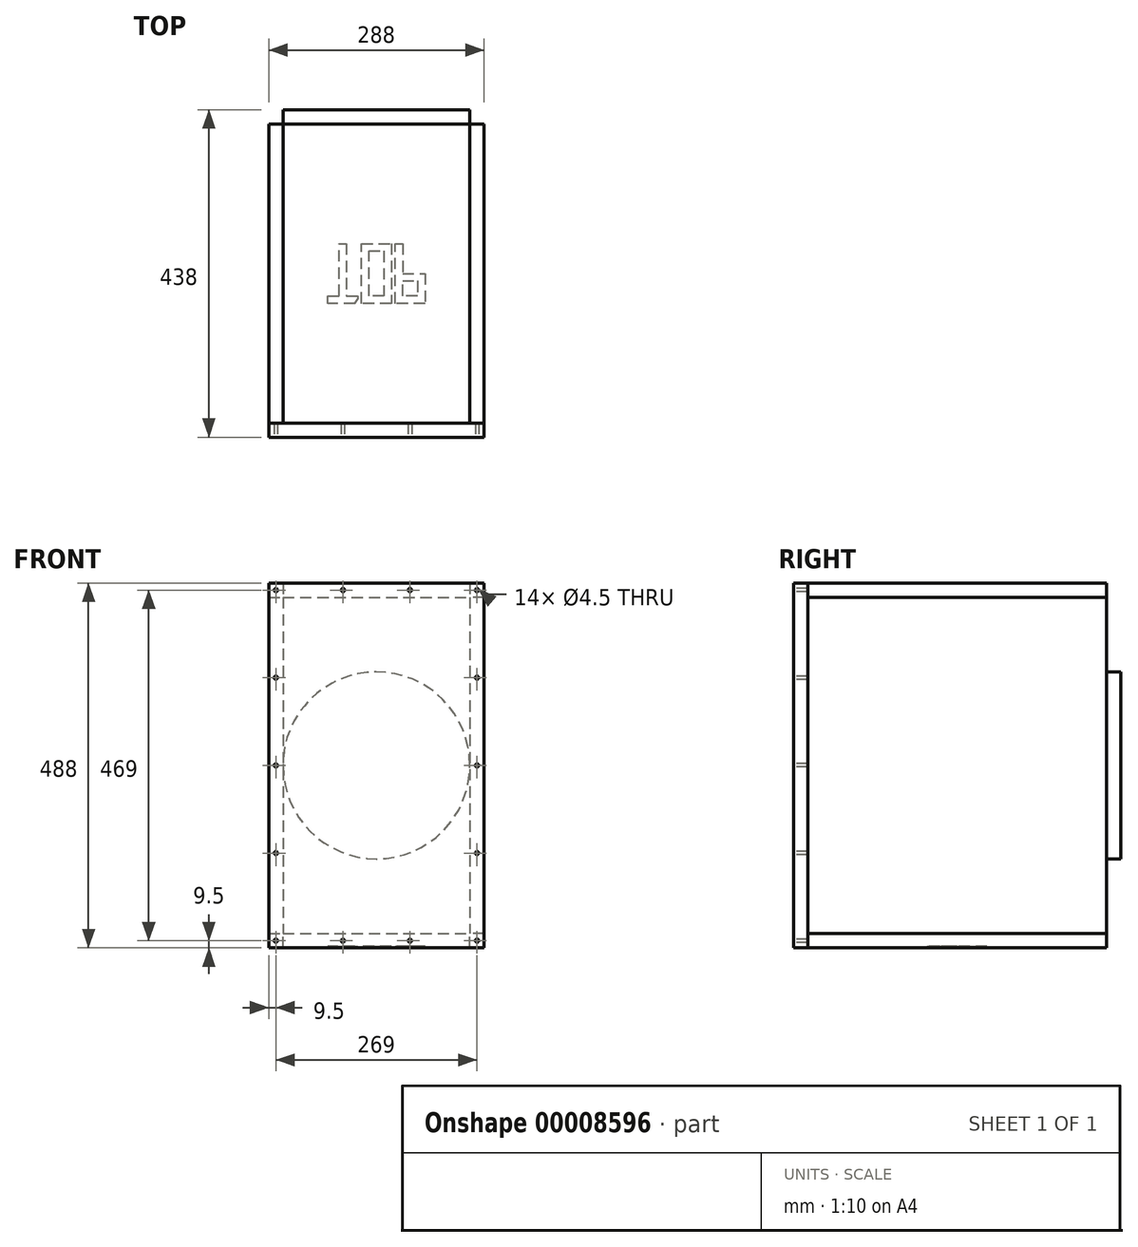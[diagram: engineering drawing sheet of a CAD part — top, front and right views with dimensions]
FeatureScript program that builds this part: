
annotation { "Feature Type Name" : "Feature", "Feature Type Description" : "" }
export const myFeature = defineFeature(function(context is Context, id is Id, definition is map)
    precondition{}
    {
        {
            var Q0;
            Q0=qCreatedBy(makeId("Top.planeOp"),FACE);
            var sketch = newSketch(context, id + "F0", { "sketchPlane" : qUnion([Q0])});
            skLineSegment(sketch, "E0.bottom", {"start": v(-125, 200) * mm, "end": v(125, 200) * mm});
            skLineSegment(sketch, "E0.top", {"start": v(-125, -200) * mm, "end": v(125, -200) * mm});
            skLineSegment(sketch, "E0.left", {"start": v(-125, 200) * mm, "end": v(-125, -200) * mm});
            skLineSegment(sketch, "E0.right", {"start": v(125, 200) * mm, "end": v(125, -200) * mm});
            skSolve(sketch);
        }
        {
            var Q0;
            Q0=makeQuery(id+"F0.imprint","IMPRINT",FACE,{"disambiguationData":[TD([[makeQuery(id+"F0.imprint","IMPRINT",EDGE,{"derivedFrom":sQuery(id+"F0.wireOp",EDGE,"E0.bottom")}),-1.0]])]});
            extrude(context, id + "F1", {"entities" : qUnion([Q0]), "endBound" : BoundingType.SYMMETRIC, "depth" : 450 * mm});
        }
        {
            var Q0;
            Q0=makeQuery(id+"F1.opExtrude","SWEPT_FACE",FACE,{"disambiguationData":[OSD([sQuery(id+"F0.wireOp",EDGE,"E0.right")])]});
            var sketch = newSketch(context, id + "F2", { "sketchPlane" : qUnion([Q0])});
            skLineSegment(sketch, "E1.0.0", {"start": v(-200, -225) * mm, "end": v(200, -225) * mm});
            skLineSegment(sketch, "E1.0.1", {"start": v(200, -225) * mm, "end": v(200, 225) * mm});
            skLineSegment(sketch, "E1.0.2", {"start": v(200, 225) * mm, "end": v(-200, 225) * mm});
            skLineSegment(sketch, "E1.0.3", {"start": v(-200, 225) * mm, "end": v(-200, -225) * mm});
            skSolve(sketch);
        }
        {
            var Q0;
            Q0=makeQuery(id+"F2.imprint","IMPRINT",FACE,{"disambiguationData":[TD([[makeQuery(id+"F2.imprint","IMPRINT",EDGE,{"derivedFrom":sQuery(id+"F2.wireOp",EDGE,"E1.0.0")}),-1.0]])]});
            extrude(context, id + "F3", {"entities" : qUnion([Q0]), "depth" : 19 * mm});
        }
        {
            var Q0;
            Q0=makeQuery(id+"F1.opExtrude","SWEPT_FACE",FACE,{"disambiguationData":[OSD([sQuery(id+"F0.wireOp",EDGE,"E0.left")])]});
            var sketch = newSketch(context, id + "F4", { "sketchPlane" : qUnion([Q0])});
            skLineSegment(sketch, "E2.0.0", {"start": v(-200, -225) * mm, "end": v(200, -225) * mm});
            skLineSegment(sketch, "E2.0.1", {"start": v(200, -225) * mm, "end": v(200, 225) * mm});
            skLineSegment(sketch, "E2.0.2", {"start": v(200, 225) * mm, "end": v(-200, 225) * mm});
            skLineSegment(sketch, "E2.0.3", {"start": v(-200, 225) * mm, "end": v(-200, -225) * mm});
            skSolve(sketch);
        }
        {
            var Q0;
            Q0=makeQuery(id+"F4.imprint","IMPRINT",FACE,{"disambiguationData":[TD([[makeQuery(id+"F4.imprint","IMPRINT",EDGE,{"derivedFrom":sQuery(id+"F4.wireOp",EDGE,"E2.0.0")}),1.0]])]});
            extrude(context, id + "F5", {"entities" : qUnion([Q0]), "depth" : 19 * mm});
        }
        {
            var Q0;
            Q0=makeQuery(id+"F1.opExtrude","CAP_FACE",FACE,{"disambiguationData":[OSD([sQuery(id+"F0.wireOp",EDGE,"E0.bottom"),sQuery(id+"F0.wireOp",EDGE,"E0.top"),sQuery(id+"F0.wireOp",EDGE,"E0.left"),sQuery(id+"F0.wireOp",EDGE,"E0.right")])],"isStart":false});
            var sketch = newSketch(context, id + "F6", { "sketchPlane" : qUnion([Q0])});
            skLineSegment(sketch, "E3.0", {"start": v(-144, 200) * mm, "end": v(-144, -200) * mm});
            skLineSegment(sketch, "E4.0", {"start": v(144, 200) * mm, "end": v(144, -200) * mm});
            skLineSegment(sketch, "E5.bottom", {"start": v(-144, -200) * mm, "end": v(144, -200) * mm});
            skLineSegment(sketch, "E5.top", {"start": v(-144, 200) * mm, "end": v(144, 200) * mm});
            skLineSegment(sketch, "E5.left", {"start": v(-144, -200) * mm, "end": v(-144, 200) * mm});
            skLineSegment(sketch, "E5.right", {"start": v(144, -200) * mm, "end": v(144, 200) * mm});
            skSolve(sketch);
        }
        {
            var Q0;
            {var subQ1=sQuery(id+"F6.wireOp",EDGE,"E5.left");Q0=makeQuery(id+"F6.imprint","IMPRINT",FACE,{"disambiguationData":[TD([[makeQuery(id+"F6.imprint","IMPRINT",EDGE,{"derivedFrom":subQ1}),-1.0]])]});}
            var Q1;
            {var subQ1=makeQuery(id+"F1.opExtrude","CAP_EDGE",EDGE,{"disambiguationData":[OSD([sQuery(id+"F0.wireOp",EDGE,"E0.left")])],"isStart":false});Q1=makeQuery(id+"F6.imprint","IMPRINT",FACE,{"disambiguationData":[TD([[makeQuery(id+"F6.imprint","IMPRINT",EDGE,{"derivedFrom":subQ1}),1.0]])]});}
            var Q2;
            {var subQ1=sQuery(id+"F6.wireOp",EDGE,"E5.right");Q2=makeQuery(id+"F6.imprint","IMPRINT",FACE,{"disambiguationData":[TD([[makeQuery(id+"F6.imprint","IMPRINT",EDGE,{"derivedFrom":subQ1}),1.0]])]});}
            extrude(context, id + "F7", {"entities" : qUnion([Q0, Q1, Q2]), "depth" : 19 * mm});
        }
        {
            var Q0;
            Q0=makeQuery(id+"F1.opExtrude","CAP_FACE",FACE,{"disambiguationData":[OSD([sQuery(id+"F0.wireOp",EDGE,"E0.bottom"),sQuery(id+"F0.wireOp",EDGE,"E0.top"),sQuery(id+"F0.wireOp",EDGE,"E0.left"),sQuery(id+"F0.wireOp",EDGE,"E0.right")])],"isStart":true});
            var sketch = newSketch(context, id + "F8", { "sketchPlane" : qUnion([Q0])});
            skLineSegment(sketch, "E6.0", {"start": v(144, -200) * mm, "end": v(144, 200) * mm});
            skLineSegment(sketch, "E7.0", {"start": v(-144, -200) * mm, "end": v(-144, 200) * mm});
            skLineSegment(sketch, "E8.bottom", {"start": v(144, 200) * mm, "end": v(-144, 200) * mm});
            skLineSegment(sketch, "E8.top", {"start": v(144, -200) * mm, "end": v(-144, -200) * mm});
            skLineSegment(sketch, "E8.left", {"start": v(144, 200) * mm, "end": v(144, -200) * mm});
            skLineSegment(sketch, "E8.right", {"start": v(-144, 200) * mm, "end": v(-144, -200) * mm});
            skSolve(sketch);
        }
        {
            var Q0;
            {var subQ1=sQuery(id+"F8.wireOp",EDGE,"E8.left");Q0=makeQuery(id+"F8.imprint","IMPRINT",FACE,{"disambiguationData":[TD([[makeQuery(id+"F8.imprint","IMPRINT",EDGE,{"derivedFrom":subQ1}),-1.0]])]});}
            var Q1;
            {var subQ1=makeQuery(id+"F1.opExtrude","CAP_EDGE",EDGE,{"disambiguationData":[OSD([sQuery(id+"F0.wireOp",EDGE,"E0.left")])],"isStart":true});Q1=makeQuery(id+"F8.imprint","IMPRINT",FACE,{"disambiguationData":[TD([[makeQuery(id+"F8.imprint","IMPRINT",EDGE,{"derivedFrom":subQ1}),-1.0]])]});}
            var Q2;
            {var subQ1=sQuery(id+"F8.wireOp",EDGE,"E8.right");Q2=makeQuery(id+"F8.imprint","IMPRINT",FACE,{"disambiguationData":[TD([[makeQuery(id+"F8.imprint","IMPRINT",EDGE,{"derivedFrom":subQ1}),1.0]])]});}
            extrude(context, id + "F9", {"entities" : qUnion([Q0, Q1, Q2]), "depth" : 19 * mm});
        }
        {
            var Q0;
            Q0=makeQuery(id+"F1.opExtrude","SWEPT_FACE",FACE,{"disambiguationData":[OSD([sQuery(id+"F0.wireOp",EDGE,"E0.bottom")])]});
            var sketch = newSketch(context, id + "F10", { "sketchPlane" : qUnion([Q0])});
            skLineSegment(sketch, "E9.0", {"start": v(-144, -244) * mm, "end": v(-144, -225) * mm});
            skLineSegment(sketch, "E10.0", {"start": v(144, 244) * mm, "end": v(144, 225) * mm});
            skLineSegment(sketch, "E11.bottom", {"start": v(-144, -244) * mm, "end": v(144, -244) * mm});
            skLineSegment(sketch, "E11.top", {"start": v(-144, 244) * mm, "end": v(144, 244) * mm});
            skLineSegment(sketch, "E11.left", {"start": v(-144, -244) * mm, "end": v(-144, 244) * mm});
            skLineSegment(sketch, "E11.right", {"start": v(144, -244) * mm, "end": v(144, 244) * mm});
            skSolve(sketch);
        }
        {
            var Q0;
            {var subQ3=sQuery(id+"F10.wireOp",EDGE,"E11.bottom");Q0=makeQuery(id+"F10.imprint","IMPRINT",FACE,{"disambiguationData":[TD([[makeQuery(id+"F10.imprint","IMPRINT",EDGE,{"derivedFrom":subQ3}),1.0]])]});}
            var Q1;
            {var subQ0=sQuery(id+"F0.wireOp",EDGE,"E0.bottom");Q1=makeQuery(id+"F10.imprint","IMPRINT",FACE,{"disambiguationData":[TD([[makeQuery(id+"F10.imprint","IMPRINT",EDGE,{"derivedFrom":makeQuery(id+"F1.opExtrude","CAP_EDGE",EDGE,{"disambiguationData":[OSD([subQ0])],"isStart":true})}),-1.0]])]});}
            extrude(context, id + "F11", {"entities" : qUnion([Q0, Q1]), "depth" : 19 * mm});
        }
        {
            var Q0;
            Q0=makeQuery(id+"F1.opExtrude","SWEPT_FACE",FACE,{"disambiguationData":[OSD([sQuery(id+"F0.wireOp",EDGE,"E0.top")])]});
            var sketch = newSketch(context, id + "F12", { "sketchPlane" : qUnion([Q0])});
            skLineSegment(sketch, "E12.0", {"start": v(144, 244) * mm, "end": v(144, 225) * mm});
            skLineSegment(sketch, "E13.0", {"start": v(-144, -244) * mm, "end": v(-144, -225) * mm});
            skLineSegment(sketch, "E14.bottom", {"start": v(144, 244) * mm, "end": v(-144, 244) * mm});
            skLineSegment(sketch, "E14.top", {"start": v(144, -244) * mm, "end": v(-144, -244) * mm});
            skLineSegment(sketch, "E14.left", {"start": v(144, 244) * mm, "end": v(144, -244) * mm});
            skLineSegment(sketch, "E14.right", {"start": v(-144, 244) * mm, "end": v(-144, -244) * mm});
            skSolve(sketch);
        }
        {
            var Q0;
            {var subQ0=sQuery(id+"F0.wireOp",EDGE,"E0.top");Q0=makeQuery(id+"F12.imprint","IMPRINT",FACE,{"disambiguationData":[TD([[makeQuery(id+"F12.imprint","IMPRINT",EDGE,{"derivedFrom":makeQuery(id+"F1.opExtrude","CAP_EDGE",EDGE,{"disambiguationData":[OSD([subQ0])],"isStart":true})}),1.0]])]});}
            var Q1;
            {var subQ3=sQuery(id+"F12.wireOp",EDGE,"E14.bottom");Q1=makeQuery(id+"F12.imprint","IMPRINT",FACE,{"disambiguationData":[TD([[makeQuery(id+"F12.imprint","IMPRINT",EDGE,{"derivedFrom":subQ3}),1.0]])]});}
            extrude(context, id + "F13", {"entities" : qUnion([Q0, Q1]), "depth" : 19 * mm});
        }
        {
            var Q0;
            Q0=makeQuery(id+"F9.opExtrude","CAP_FACE",FACE,{"disambiguationData":[OSD([sQuery(id+"F8.wireOp",EDGE,"E8.bottom"),sQuery(id+"F8.wireOp",EDGE,"E8.top"),sQuery(id+"F8.wireOp",EDGE,"E8.left"),sQuery(id+"F8.wireOp",EDGE,"E8.right")])],"isStart":false});
            var sketch = newSketch(context, id + "F14", { "sketchPlane" : qUnion([Q0])});
            skLineSegment(sketch, "E15", {"start": v(-50, 30) * mm, "end": v(-50, -40) * mm});
            skLineSegment(sketch, "E16", {"start": v(-50, -40) * mm, "end": v(-40, -40) * mm});
            skLineSegment(sketch, "E17", {"start": v(-40, -40) * mm, "end": v(-40, 30) * mm});
            skLineSegment(sketch, "E18", {"start": v(-40, 30) * mm, "end": v(-25, 30) * mm});
            skLineSegment(sketch, "E19", {"start": v(-25, 30) * mm, "end": v(-25, 40) * mm});
            skLineSegment(sketch, "E20", {"start": v(-25, 40) * mm, "end": v(-65, 40) * mm});
            skLineSegment(sketch, "E21", {"start": v(-65, 40) * mm, "end": v(-65, 30) * mm});
            skLineSegment(sketch, "E22", {"start": v(-65, 30) * mm, "end": v(-50, 30) * mm});
            skLineSegment(sketch, "E23", {"start": v(-20, 40) * mm, "end": v(-20, -40) * mm});
            skLineSegment(sketch, "E24", {"start": v(-20, -40) * mm, "end": v(20, -40) * mm});
            skLineSegment(sketch, "E25", {"start": v(20, -40) * mm, "end": v(20, 40) * mm});
            skLineSegment(sketch, "E26", {"start": v(20, 40) * mm, "end": v(-20, 40) * mm});
            skLineSegment(sketch, "E27", {"start": v(-10, 30) * mm, "end": v(-10, -30) * mm});
            skLineSegment(sketch, "E28", {"start": v(-10, -30) * mm, "end": v(10, -30) * mm});
            skLineSegment(sketch, "E29", {"start": v(10, -30) * mm, "end": v(10, 30) * mm});
            skLineSegment(sketch, "E30", {"start": v(10, 30) * mm, "end": v(-10, 30) * mm});
            skLineSegment(sketch, "E31", {"start": v(25, 40) * mm, "end": v(25, -40) * mm});
            skLineSegment(sketch, "E32", {"start": v(25, -40) * mm, "end": v(35, -40) * mm});
            skLineSegment(sketch, "E33", {"start": v(35, -40) * mm, "end": v(35, 0) * mm});
            skLineSegment(sketch, "E34", {"start": v(35, 0) * mm, "end": v(65, 0) * mm});
            skLineSegment(sketch, "E35", {"start": v(65, 0) * mm, "end": v(65, 40) * mm});
            skLineSegment(sketch, "E36", {"start": v(65, 40) * mm, "end": v(25, 40) * mm});
            skLineSegment(sketch, "E37", {"start": v(35, 30) * mm, "end": v(35, 10) * mm});
            skLineSegment(sketch, "E38", {"start": v(35, 10) * mm, "end": v(55, 10) * mm});
            skLineSegment(sketch, "E39", {"start": v(55, 10) * mm, "end": v(55, 30) * mm});
            skLineSegment(sketch, "E40", {"start": v(55, 30) * mm, "end": v(35, 30) * mm});
            skLineSegment(sketch, "E41", {"start": v(-144, 200) * mm, "end": v(0, 0) * mm});
            skLineSegment(sketch, "E42", {"start": v(-10, -30) * mm, "end": v(10, 30) * mm});
            skLineSegment(sketch, "E43", {"start": v(0, 0) * mm, "end": v(144, -200) * mm});
            skSolve(sketch);
        }
        {
            var Q0;
            Q0=makeQuery(id+"F14.imprint","IMPRINT",FACE,{"disambiguationData":[TD([[makeQuery(id+"F14.imprint","IMPRINT",EDGE,{"derivedFrom":sQuery(id+"F14.wireOp",EDGE,"E15")}),1.0]])]});
            var Q1;
            {var subQ6=sQuery(id+"F14.wireOp",EDGE,"E18");Q1=makeQuery(id+"F14.imprint","IMPRINT",FACE,{"disambiguationData":[TD([[makeQuery(id+"F14.imprint","IMPRINT",EDGE,{"derivedFrom":subQ6}),1.0]])]});}
            var Q2;
            {var subQ11=sQuery(id+"F14.wireOp",EDGE,"E26");Q2=makeQuery(id+"F14.imprint","IMPRINT",FACE,{"disambiguationData":[TD([[makeQuery(id+"F14.imprint","IMPRINT",EDGE,{"derivedFrom":subQ11}),1.0]])]});}
            var Q3;
            {var subQ9=sQuery(id+"F14.wireOp",EDGE,"E24");Q3=makeQuery(id+"F14.imprint","IMPRINT",FACE,{"disambiguationData":[TD([[makeQuery(id+"F14.imprint","IMPRINT",EDGE,{"derivedFrom":subQ9}),1.0]])]});}
            var Q4;
            {var subQ5=sQuery(id+"F14.wireOp",EDGE,"E32");Q4=makeQuery(id+"F14.imprint","IMPRINT",FACE,{"disambiguationData":[TD([[makeQuery(id+"F14.imprint","IMPRINT",EDGE,{"derivedFrom":subQ5}),1.0]])]});}
            var Q5;
            {var subQ6=sQuery(id+"F14.wireOp",EDGE,"E34");Q5=makeQuery(id+"F14.imprint","IMPRINT",FACE,{"disambiguationData":[TD([[makeQuery(id+"F14.imprint","IMPRINT",EDGE,{"derivedFrom":subQ6}),1.0]])]});}
            extrude(context, id + "F15", {"entities" : qUnion([Q0, Q1, Q2, Q3, Q4, Q5]), "operationType" : NewBodyOperationType.REMOVE, "oppositeDirection" : true, "depth" : 2 * mm});
        }
        {
            var Q0;
            Q0=makeQuery(id+"F11.opExtrude","CAP_FACE",FACE,{"disambiguationData":[OSD([sQuery(id+"F10.wireOp",EDGE,"E11.bottom"),sQuery(id+"F10.wireOp",EDGE,"E11.top"),sQuery(id+"F10.wireOp",EDGE,"E11.left"),sQuery(id+"F10.wireOp",EDGE,"E11.right")])],"isStart":false});
            var sketch = newSketch(context, id + "F16", { "sketchPlane" : qUnion([Q0])});
            skLineSegment(sketch, "E44", {"start": v(-144, -244) * mm, "end": v(144, 244) * mm});
            skCircle(sketch, "E45", {"center": v(0, 0) * mm, "radius": 125 * mm});
            skSolve(sketch);
        }
        {
            var Q0;
            {var subQ0=sQuery(id+"F16.wireOp",EDGE,"E45");var subQ1=sQuery(id+"F16.wireOp",EDGE,"E44");var subQ3=makeQuery(id+"F16.imprint","INTERSECT",VERTEX,{"disambiguationData":[OD(0.0)],"derivedFrom":[subQ1,subQ0]});Q0=makeQuery(id+"F16.imprint","IMPRINT",FACE,{"disambiguationData":[TD([[makeQuery(id+"F16.imprint","IMPRINT",EDGE,{"disambiguationData":[TD([[subQ3,-1.0]])],"derivedFrom":subQ1}),1.0]])]});}
            var Q1;
            {var subQ0=sQuery(id+"F16.wireOp",EDGE,"E45");var subQ1=sQuery(id+"F16.wireOp",EDGE,"E44");var subQ3=makeQuery(id+"F16.imprint","INTERSECT",VERTEX,{"disambiguationData":[OD(0.0)],"derivedFrom":[subQ1,subQ0]});Q1=makeQuery(id+"F16.imprint","IMPRINT",FACE,{"disambiguationData":[TD([[makeQuery(id+"F16.imprint","IMPRINT",EDGE,{"disambiguationData":[TD([[subQ3,-1.0]])],"derivedFrom":subQ1}),-1.0]])]});}
            extrude(context, id + "F17", {"entities" : qUnion([Q0, Q1]), "operationType" : NewBodyOperationType.REMOVE, "endBound" : BoundingType.UP_TO_NEXT, "oppositeDirection" : true, "depth" : 25 * mm});
        }
        {
            var Q0;
            Q0=makeQuery(id+"F11.opExtrude","CAP_FACE",FACE,{"disambiguationData":[OSD([sQuery(id+"F10.wireOp",EDGE,"E11.bottom"),sQuery(id+"F10.wireOp",EDGE,"E11.top"),sQuery(id+"F10.wireOp",EDGE,"E11.left"),sQuery(id+"F10.wireOp",EDGE,"E11.right")])],"isStart":false});
            var sketch = newSketch(context, id + "F18", { "sketchPlane" : qUnion([Q0])});
            skLineSegment(sketch, "E46.0.0", {"start": v(-144, 244) * mm, "end": v(-144, -244) * mm});
            skLineSegment(sketch, "E46.0.1", {"start": v(-144, -244) * mm, "end": v(144, -244) * mm});
            skLineSegment(sketch, "E46.0.2", {"start": v(144, -244) * mm, "end": v(144, 244) * mm});
            skLineSegment(sketch, "E46.0.3", {"start": v(144, 244) * mm, "end": v(-144, 244) * mm});
            skCircle(sketch, "E47", {"center": v(-44.83, 234.5) * mm, "radius": 2.25 * mm});
            skCircle(sketch, "E48", {"center": v(44.83, 234.5) * mm, "radius": 2.25 * mm});
            skCircle(sketch, "E49", {"center": v(-44.83, -234.5) * mm, "radius": 2.25 * mm});
            skCircle(sketch, "E50", {"center": v(44.83, -234.5) * mm, "radius": 2.25 * mm});
            skCircle(sketch, "E51", {"center": v(-134.5, -117.25) * mm, "radius": 2.25 * mm});
            skCircle(sketch, "E52", {"center": v(-134.5, 117.25) * mm, "radius": 2.25 * mm});
            skCircle(sketch, "E53", {"center": v(134.5, -117.25) * mm, "radius": 2.25 * mm});
            skCircle(sketch, "E54", {"center": v(134.5, 0) * mm, "radius": 2.25 * mm});
            skCircle(sketch, "E55", {"center": v(134.5, 117.25) * mm, "radius": 2.25 * mm});
            skCircle(sketch, "E56", {"center": v(-134.5, 0) * mm, "radius": 2.25 * mm});
            skLineSegment(sketch, "E57.left", {"start": v(-134.5, 234.5) * mm, "end": v(-134.5, 117.25) * mm});
            skLineSegment(sketch, "E57.right", {"start": v(134.5, 234.5) * mm, "end": v(134.5, 117.25) * mm});
            skLineSegment(sketch, "E58.right", {"start": v(-134.5, 117.25) * mm, "end": v(-134.5, 0) * mm});
            skLineSegment(sketch, "E59.left", {"start": v(-134.5, 0) * mm, "end": v(-134.5, -117.25) * mm});
            skLineSegment(sketch, "E60.left", {"start": v(134.5, -117.25) * mm, "end": v(134.5, -234.5) * mm});
            skLineSegment(sketch, "E60.right", {"start": v(-134.5, -117.25) * mm, "end": v(-134.5, -234.5) * mm});
            skLineSegment(sketch, "E61", {"start": v(-134.5, 234.5) * mm, "end": v(-44.83, 234.5) * mm});
            skLineSegment(sketch, "E62", {"start": v(-44.83, 234.5) * mm, "end": v(44.83, 234.5) * mm});
            skLineSegment(sketch, "E63", {"start": v(44.83, 234.5) * mm, "end": v(134.5, 234.5) * mm});
            skLineSegment(sketch, "E64", {"start": v(-134.5, -234.5) * mm, "end": v(-44.83, -234.5) * mm});
            skLineSegment(sketch, "E65", {"start": v(-44.83, -234.5) * mm, "end": v(44.83, -234.5) * mm});
            skLineSegment(sketch, "E66", {"start": v(44.83, -234.5) * mm, "end": v(134.5, -234.5) * mm});
            skLineSegment(sketch, "E67", {"start": v(134.5, 117.25) * mm, "end": v(134.5, 0) * mm});
            skLineSegment(sketch, "E68", {"start": v(134.5, 0) * mm, "end": v(134.5, -117.25) * mm});
            skCircle(sketch, "E69", {"center": v(-134.5, 234.5) * mm, "radius": 2.25 * mm});
            skCircle(sketch, "E70", {"center": v(134.5, 234.5) * mm, "radius": 2.25 * mm});
            skCircle(sketch, "E71", {"center": v(134.5, -234.5) * mm, "radius": 2.25 * mm});
            skCircle(sketch, "E72", {"center": v(-134.5, -234.5) * mm, "radius": 2.25 * mm});
            skSolve(sketch);
        }
        {
            var Q0;
            {var subQ1=sQuery(id+"F18.wireOp",EDGE,"E61");var subQ3=sQuery(id+"F18.wireOp",EDGE,"E57.left");var subQ5=makeQuery(id+"F18.imprint","INTERSECT",VERTEX,{"derivedFrom":[subQ3,subQ1]});Q0=makeQuery(id+"F18.imprint","IMPRINT",FACE,{"disambiguationData":[TD([[makeQuery(id+"F18.imprint","IMPRINT",EDGE,{"disambiguationData":[TD([[subQ5,-1.0]])],"derivedFrom":subQ3}),-1.0]])]});}
            var Q1;
            {var subQ1=sQuery(id+"F18.wireOp",EDGE,"E61");var subQ3=sQuery(id+"F18.wireOp",EDGE,"E57.left");var subQ5=makeQuery(id+"F18.imprint","INTERSECT",VERTEX,{"derivedFrom":[subQ3,subQ1]});Q1=makeQuery(id+"F18.imprint","IMPRINT",FACE,{"disambiguationData":[TD([[makeQuery(id+"F18.imprint","IMPRINT",EDGE,{"disambiguationData":[TD([[subQ5,-1.0]])],"derivedFrom":subQ3}),1.0]])]});}
            var Q2;
            {var subQ1=sQuery(id+"F18.wireOp",EDGE,"E47");var subQ3=sQuery(id+"F18.wireOp",EDGE,"E61");var subQ5=makeQuery(id+"F18.imprint","INTERSECT",VERTEX,{"derivedFrom":[subQ1,subQ3]});Q2=makeQuery(id+"F18.imprint","IMPRINT",FACE,{"disambiguationData":[TD([[makeQuery(id+"F18.imprint","IMPRINT",EDGE,{"disambiguationData":[TD([[subQ5,-1.0]])],"derivedFrom":subQ1}),1.0]])]});}
            var Q3;
            {var subQ1=sQuery(id+"F18.wireOp",EDGE,"E47");var subQ3=sQuery(id+"F18.wireOp",EDGE,"E61");var subQ5=makeQuery(id+"F18.imprint","INTERSECT",VERTEX,{"derivedFrom":[subQ1,subQ3]});Q3=makeQuery(id+"F18.imprint","IMPRINT",FACE,{"disambiguationData":[TD([[makeQuery(id+"F18.imprint","IMPRINT",EDGE,{"disambiguationData":[TD([[subQ5,1.0]])],"derivedFrom":subQ1}),1.0]])]});}
            var Q4;
            {var subQ1=sQuery(id+"F18.wireOp",EDGE,"E48");var subQ3=sQuery(id+"F18.wireOp",EDGE,"E62");var subQ5=makeQuery(id+"F18.imprint","INTERSECT",VERTEX,{"derivedFrom":[subQ1,subQ3]});Q4=makeQuery(id+"F18.imprint","IMPRINT",FACE,{"disambiguationData":[TD([[makeQuery(id+"F18.imprint","IMPRINT",EDGE,{"disambiguationData":[TD([[subQ5,1.0]])],"derivedFrom":subQ1}),1.0]])]});}
            var Q5;
            {var subQ1=sQuery(id+"F18.wireOp",EDGE,"E48");var subQ3=sQuery(id+"F18.wireOp",EDGE,"E62");var subQ5=makeQuery(id+"F18.imprint","INTERSECT",VERTEX,{"derivedFrom":[subQ1,subQ3]});Q5=makeQuery(id+"F18.imprint","IMPRINT",FACE,{"disambiguationData":[TD([[makeQuery(id+"F18.imprint","IMPRINT",EDGE,{"disambiguationData":[TD([[subQ5,-1.0]])],"derivedFrom":subQ1}),1.0]])]});}
            var Q6;
            {var subQ1=sQuery(id+"F18.wireOp",EDGE,"E63");var subQ3=sQuery(id+"F18.wireOp",EDGE,"E57.right");var subQ5=makeQuery(id+"F18.imprint","INTERSECT",VERTEX,{"derivedFrom":[subQ3,subQ1]});Q6=makeQuery(id+"F18.imprint","IMPRINT",FACE,{"disambiguationData":[TD([[makeQuery(id+"F18.imprint","IMPRINT",EDGE,{"disambiguationData":[TD([[subQ5,-1.0]])],"derivedFrom":subQ3}),1.0]])]});}
            var Q7;
            {var subQ1=sQuery(id+"F18.wireOp",EDGE,"E63");var subQ3=sQuery(id+"F18.wireOp",EDGE,"E57.right");var subQ5=makeQuery(id+"F18.imprint","INTERSECT",VERTEX,{"derivedFrom":[subQ3,subQ1]});Q7=makeQuery(id+"F18.imprint","IMPRINT",FACE,{"disambiguationData":[TD([[makeQuery(id+"F18.imprint","IMPRINT",EDGE,{"disambiguationData":[TD([[subQ5,-1.0]])],"derivedFrom":subQ3}),-1.0]])]});}
            var Q8;
            {var subQ1=sQuery(id+"F18.wireOp",EDGE,"E55");var subQ3=sQuery(id+"F18.wireOp",EDGE,"E57.right");var subQ5=makeQuery(id+"F18.imprint","INTERSECT",VERTEX,{"derivedFrom":[subQ1,subQ3]});Q8=makeQuery(id+"F18.imprint","IMPRINT",FACE,{"disambiguationData":[TD([[makeQuery(id+"F18.imprint","IMPRINT",EDGE,{"disambiguationData":[TD([[subQ5,-1.0]])],"derivedFrom":subQ1}),1.0]])]});}
            var Q9;
            {var subQ1=sQuery(id+"F18.wireOp",EDGE,"E55");var subQ3=sQuery(id+"F18.wireOp",EDGE,"E57.right");var subQ5=makeQuery(id+"F18.imprint","INTERSECT",VERTEX,{"derivedFrom":[subQ1,subQ3]});Q9=makeQuery(id+"F18.imprint","IMPRINT",FACE,{"disambiguationData":[TD([[makeQuery(id+"F18.imprint","IMPRINT",EDGE,{"disambiguationData":[TD([[subQ5,1.0]])],"derivedFrom":subQ1}),1.0]])]});}
            var Q10;
            {var subQ1=sQuery(id+"F18.wireOp",EDGE,"E54");var subQ3=sQuery(id+"F18.wireOp",EDGE,"E67");var subQ5=makeQuery(id+"F18.imprint","INTERSECT",VERTEX,{"derivedFrom":[subQ1,subQ3]});Q10=makeQuery(id+"F18.imprint","IMPRINT",FACE,{"disambiguationData":[TD([[makeQuery(id+"F18.imprint","IMPRINT",EDGE,{"disambiguationData":[TD([[subQ5,-1.0]])],"derivedFrom":subQ1}),1.0]])]});}
            var Q11;
            {var subQ1=sQuery(id+"F18.wireOp",EDGE,"E54");var subQ3=sQuery(id+"F18.wireOp",EDGE,"E67");var subQ5=makeQuery(id+"F18.imprint","INTERSECT",VERTEX,{"derivedFrom":[subQ1,subQ3]});Q11=makeQuery(id+"F18.imprint","IMPRINT",FACE,{"disambiguationData":[TD([[makeQuery(id+"F18.imprint","IMPRINT",EDGE,{"disambiguationData":[TD([[subQ5,1.0]])],"derivedFrom":subQ1}),1.0]])]});}
            var Q12;
            {var subQ1=sQuery(id+"F18.wireOp",EDGE,"E53");var subQ3=sQuery(id+"F18.wireOp",EDGE,"E60.left");var subQ5=makeQuery(id+"F18.imprint","INTERSECT",VERTEX,{"derivedFrom":[subQ1,subQ3]});Q12=makeQuery(id+"F18.imprint","IMPRINT",FACE,{"disambiguationData":[TD([[makeQuery(id+"F18.imprint","IMPRINT",EDGE,{"disambiguationData":[TD([[subQ5,1.0]])],"derivedFrom":subQ1}),1.0]])]});}
            var Q13;
            {var subQ1=sQuery(id+"F18.wireOp",EDGE,"E53");var subQ3=sQuery(id+"F18.wireOp",EDGE,"E60.left");var subQ5=makeQuery(id+"F18.imprint","INTERSECT",VERTEX,{"derivedFrom":[subQ1,subQ3]});Q13=makeQuery(id+"F18.imprint","IMPRINT",FACE,{"disambiguationData":[TD([[makeQuery(id+"F18.imprint","IMPRINT",EDGE,{"disambiguationData":[TD([[subQ5,-1.0]])],"derivedFrom":subQ1}),1.0]])]});}
            var Q14;
            {var subQ1=sQuery(id+"F18.wireOp",EDGE,"E66");var subQ3=sQuery(id+"F18.wireOp",EDGE,"E60.left");var subQ5=makeQuery(id+"F18.imprint","INTERSECT",VERTEX,{"derivedFrom":[subQ3,subQ1]});Q14=makeQuery(id+"F18.imprint","IMPRINT",FACE,{"disambiguationData":[TD([[makeQuery(id+"F18.imprint","IMPRINT",EDGE,{"disambiguationData":[TD([[subQ5,1.0]])],"derivedFrom":subQ3}),-1.0]])]});}
            var Q15;
            {var subQ1=sQuery(id+"F18.wireOp",EDGE,"E66");var subQ3=sQuery(id+"F18.wireOp",EDGE,"E60.left");var subQ5=makeQuery(id+"F18.imprint","INTERSECT",VERTEX,{"derivedFrom":[subQ3,subQ1]});Q15=makeQuery(id+"F18.imprint","IMPRINT",FACE,{"disambiguationData":[TD([[makeQuery(id+"F18.imprint","IMPRINT",EDGE,{"disambiguationData":[TD([[subQ5,1.0]])],"derivedFrom":subQ3}),1.0]])]});}
            var Q16;
            {var subQ1=sQuery(id+"F18.wireOp",EDGE,"E50");var subQ3=sQuery(id+"F18.wireOp",EDGE,"E65");var subQ5=makeQuery(id+"F18.imprint","INTERSECT",VERTEX,{"derivedFrom":[subQ1,subQ3]});Q16=makeQuery(id+"F18.imprint","IMPRINT",FACE,{"disambiguationData":[TD([[makeQuery(id+"F18.imprint","IMPRINT",EDGE,{"disambiguationData":[TD([[subQ5,1.0]])],"derivedFrom":subQ1}),1.0]])]});}
            var Q17;
            {var subQ1=sQuery(id+"F18.wireOp",EDGE,"E50");var subQ3=sQuery(id+"F18.wireOp",EDGE,"E65");var subQ5=makeQuery(id+"F18.imprint","INTERSECT",VERTEX,{"derivedFrom":[subQ1,subQ3]});Q17=makeQuery(id+"F18.imprint","IMPRINT",FACE,{"disambiguationData":[TD([[makeQuery(id+"F18.imprint","IMPRINT",EDGE,{"disambiguationData":[TD([[subQ5,-1.0]])],"derivedFrom":subQ1}),1.0]])]});}
            var Q18;
            {var subQ1=sQuery(id+"F18.wireOp",EDGE,"E49");var subQ3=sQuery(id+"F18.wireOp",EDGE,"E64");var subQ5=makeQuery(id+"F18.imprint","INTERSECT",VERTEX,{"derivedFrom":[subQ1,subQ3]});Q18=makeQuery(id+"F18.imprint","IMPRINT",FACE,{"disambiguationData":[TD([[makeQuery(id+"F18.imprint","IMPRINT",EDGE,{"disambiguationData":[TD([[subQ5,-1.0]])],"derivedFrom":subQ1}),1.0]])]});}
            var Q19;
            {var subQ1=sQuery(id+"F18.wireOp",EDGE,"E49");var subQ3=sQuery(id+"F18.wireOp",EDGE,"E64");var subQ5=makeQuery(id+"F18.imprint","INTERSECT",VERTEX,{"derivedFrom":[subQ1,subQ3]});Q19=makeQuery(id+"F18.imprint","IMPRINT",FACE,{"disambiguationData":[TD([[makeQuery(id+"F18.imprint","IMPRINT",EDGE,{"disambiguationData":[TD([[subQ5,1.0]])],"derivedFrom":subQ1}),1.0]])]});}
            var Q20;
            {var subQ1=sQuery(id+"F18.wireOp",EDGE,"E64");var subQ3=sQuery(id+"F18.wireOp",EDGE,"E60.right");var subQ5=makeQuery(id+"F18.imprint","INTERSECT",VERTEX,{"derivedFrom":[subQ3,subQ1]});Q20=makeQuery(id+"F18.imprint","IMPRINT",FACE,{"disambiguationData":[TD([[makeQuery(id+"F18.imprint","IMPRINT",EDGE,{"disambiguationData":[TD([[subQ5,1.0]])],"derivedFrom":subQ3}),1.0]])]});}
            var Q21;
            {var subQ1=sQuery(id+"F18.wireOp",EDGE,"E64");var subQ3=sQuery(id+"F18.wireOp",EDGE,"E60.right");var subQ5=makeQuery(id+"F18.imprint","INTERSECT",VERTEX,{"derivedFrom":[subQ3,subQ1]});Q21=makeQuery(id+"F18.imprint","IMPRINT",FACE,{"disambiguationData":[TD([[makeQuery(id+"F18.imprint","IMPRINT",EDGE,{"disambiguationData":[TD([[subQ5,1.0]])],"derivedFrom":subQ3}),-1.0]])]});}
            var Q22;
            {var subQ1=sQuery(id+"F18.wireOp",EDGE,"E51");var subQ3=sQuery(id+"F18.wireOp",EDGE,"E59.left");var subQ5=makeQuery(id+"F18.imprint","INTERSECT",VERTEX,{"derivedFrom":[subQ1,subQ3]});Q22=makeQuery(id+"F18.imprint","IMPRINT",FACE,{"disambiguationData":[TD([[makeQuery(id+"F18.imprint","IMPRINT",EDGE,{"disambiguationData":[TD([[subQ5,-1.0]])],"derivedFrom":subQ1}),1.0]])]});}
            var Q23;
            {var subQ1=sQuery(id+"F18.wireOp",EDGE,"E51");var subQ3=sQuery(id+"F18.wireOp",EDGE,"E59.left");var subQ5=makeQuery(id+"F18.imprint","INTERSECT",VERTEX,{"derivedFrom":[subQ1,subQ3]});Q23=makeQuery(id+"F18.imprint","IMPRINT",FACE,{"disambiguationData":[TD([[makeQuery(id+"F18.imprint","IMPRINT",EDGE,{"disambiguationData":[TD([[subQ5,1.0]])],"derivedFrom":subQ1}),1.0]])]});}
            var Q24;
            {var subQ1=sQuery(id+"F18.wireOp",EDGE,"E56");var subQ3=sQuery(id+"F18.wireOp",EDGE,"E58.right");var subQ5=makeQuery(id+"F18.imprint","INTERSECT",VERTEX,{"derivedFrom":[subQ1,subQ3]});Q24=makeQuery(id+"F18.imprint","IMPRINT",FACE,{"disambiguationData":[TD([[makeQuery(id+"F18.imprint","IMPRINT",EDGE,{"disambiguationData":[TD([[subQ5,-1.0]])],"derivedFrom":subQ1}),1.0]])]});}
            var Q25;
            {var subQ1=sQuery(id+"F18.wireOp",EDGE,"E56");var subQ3=sQuery(id+"F18.wireOp",EDGE,"E58.right");var subQ5=makeQuery(id+"F18.imprint","INTERSECT",VERTEX,{"derivedFrom":[subQ1,subQ3]});Q25=makeQuery(id+"F18.imprint","IMPRINT",FACE,{"disambiguationData":[TD([[makeQuery(id+"F18.imprint","IMPRINT",EDGE,{"disambiguationData":[TD([[subQ5,1.0]])],"derivedFrom":subQ1}),1.0]])]});}
            var Q26;
            {var subQ1=sQuery(id+"F18.wireOp",EDGE,"E52");var subQ3=sQuery(id+"F18.wireOp",EDGE,"E57.left");var subQ5=makeQuery(id+"F18.imprint","INTERSECT",VERTEX,{"derivedFrom":[subQ1,subQ3]});Q26=makeQuery(id+"F18.imprint","IMPRINT",FACE,{"disambiguationData":[TD([[makeQuery(id+"F18.imprint","IMPRINT",EDGE,{"disambiguationData":[TD([[subQ5,-1.0]])],"derivedFrom":subQ1}),1.0]])]});}
            var Q27;
            {var subQ1=sQuery(id+"F18.wireOp",EDGE,"E52");var subQ3=sQuery(id+"F18.wireOp",EDGE,"E57.left");var subQ5=makeQuery(id+"F18.imprint","INTERSECT",VERTEX,{"derivedFrom":[subQ1,subQ3]});Q27=makeQuery(id+"F18.imprint","IMPRINT",FACE,{"disambiguationData":[TD([[makeQuery(id+"F18.imprint","IMPRINT",EDGE,{"disambiguationData":[TD([[subQ5,1.0]])],"derivedFrom":subQ1}),1.0]])]});}
            extrude(context, id + "F19", {"entities" : qUnion([Q0, Q1, Q2, Q3, Q4, Q5, Q6, Q7, Q8, Q9, Q10, Q11, Q12, Q13, Q14, Q15, Q16, Q17, Q18, Q19, Q20, Q21, Q22, Q23, Q24, Q25, Q26, Q27]), "operationType" : NewBodyOperationType.REMOVE, "endBound" : BoundingType.UP_TO_NEXT, "oppositeDirection" : true, "depth" : 25 * mm});
        }
        {
            var Q0;
            Q0=makeQuery(id+"F13.opExtrude","CAP_FACE",FACE,{"disambiguationData":[OSD([sQuery(id+"F12.wireOp",EDGE,"E14.bottom"),sQuery(id+"F12.wireOp",EDGE,"E14.top"),sQuery(id+"F12.wireOp",EDGE,"E14.left"),sQuery(id+"F12.wireOp",EDGE,"E14.right")])],"isStart":false});
            var sketch = newSketch(context, id + "F20", { "sketchPlane" : qUnion([Q0])});
            skCircle(sketch, "E73.0", {"center": v(134.5, -234.5) * mm, "radius": 2.25 * mm});
            skCircle(sketch, "E74.0", {"center": v(134.5, -117.25) * mm, "radius": 2.25 * mm});
            skCircle(sketch, "E75.0", {"center": v(134.5, 0) * mm, "radius": 2.25 * mm});
            skCircle(sketch, "E76.0", {"center": v(134.5, 117.25) * mm, "radius": 2.25 * mm});
            skCircle(sketch, "E77.0", {"center": v(134.5, 234.5) * mm, "radius": 2.25 * mm});
            skCircle(sketch, "E78.0", {"center": v(44.83, 234.5) * mm, "radius": 2.25 * mm});
            skCircle(sketch, "E79.0", {"center": v(-44.83, 234.5) * mm, "radius": 2.25 * mm});
            skCircle(sketch, "E80.0", {"center": v(-134.5, 234.5) * mm, "radius": 2.25 * mm});
            skCircle(sketch, "E81.0", {"center": v(-134.5, 117.25) * mm, "radius": 2.25 * mm});
            skCircle(sketch, "E82.0", {"center": v(-134.5, 0) * mm, "radius": 2.25 * mm});
            skCircle(sketch, "E83.0", {"center": v(-134.5, -117.25) * mm, "radius": 2.25 * mm});
            skCircle(sketch, "E84.0", {"center": v(-134.5, -234.5) * mm, "radius": 2.25 * mm});
            skCircle(sketch, "E85.0", {"center": v(-44.83, -234.5) * mm, "radius": 2.25 * mm});
            skCircle(sketch, "E86.0", {"center": v(44.83, -234.5) * mm, "radius": 2.25 * mm});
            skSolve(sketch);
        }
        {
            var Q0;
            Q0=makeQuery(id+"F20.imprint","IMPRINT",FACE,{"disambiguationData":[TD([[makeQuery(id+"F20.imprint","IMPRINT",EDGE,{"derivedFrom":sQuery(id+"F20.wireOp",EDGE,"E73.0")}),1.0]])]});
            var Q1;
            Q1=makeQuery(id+"F20.imprint","IMPRINT",FACE,{"disambiguationData":[TD([[makeQuery(id+"F20.imprint","IMPRINT",EDGE,{"derivedFrom":sQuery(id+"F20.wireOp",EDGE,"E86.0")}),1.0]])]});
            var Q2;
            Q2=makeQuery(id+"F20.imprint","IMPRINT",FACE,{"disambiguationData":[TD([[makeQuery(id+"F20.imprint","IMPRINT",EDGE,{"derivedFrom":sQuery(id+"F20.wireOp",EDGE,"E85.0")}),1.0]])]});
            var Q3;
            Q3=makeQuery(id+"F20.imprint","IMPRINT",FACE,{"disambiguationData":[TD([[makeQuery(id+"F20.imprint","IMPRINT",EDGE,{"derivedFrom":sQuery(id+"F20.wireOp",EDGE,"E84.0")}),1.0]])]});
            var Q4;
            Q4=makeQuery(id+"F20.imprint","IMPRINT",FACE,{"disambiguationData":[TD([[makeQuery(id+"F20.imprint","IMPRINT",EDGE,{"derivedFrom":sQuery(id+"F20.wireOp",EDGE,"E83.0")}),1.0]])]});
            var Q5;
            Q5=makeQuery(id+"F20.imprint","IMPRINT",FACE,{"disambiguationData":[TD([[makeQuery(id+"F20.imprint","IMPRINT",EDGE,{"derivedFrom":sQuery(id+"F20.wireOp",EDGE,"E82.0")}),1.0]])]});
            var Q6;
            Q6=makeQuery(id+"F20.imprint","IMPRINT",FACE,{"disambiguationData":[TD([[makeQuery(id+"F20.imprint","IMPRINT",EDGE,{"derivedFrom":sQuery(id+"F20.wireOp",EDGE,"E81.0")}),1.0]])]});
            var Q7;
            Q7=makeQuery(id+"F20.imprint","IMPRINT",FACE,{"disambiguationData":[TD([[makeQuery(id+"F20.imprint","IMPRINT",EDGE,{"derivedFrom":sQuery(id+"F20.wireOp",EDGE,"E80.0")}),1.0]])]});
            var Q8;
            Q8=makeQuery(id+"F20.imprint","IMPRINT",FACE,{"disambiguationData":[TD([[makeQuery(id+"F20.imprint","IMPRINT",EDGE,{"derivedFrom":sQuery(id+"F20.wireOp",EDGE,"E79.0")}),1.0]])]});
            var Q9;
            Q9=makeQuery(id+"F20.imprint","IMPRINT",FACE,{"disambiguationData":[TD([[makeQuery(id+"F20.imprint","IMPRINT",EDGE,{"derivedFrom":sQuery(id+"F20.wireOp",EDGE,"E78.0")}),1.0]])]});
            var Q10;
            Q10=makeQuery(id+"F20.imprint","IMPRINT",FACE,{"disambiguationData":[TD([[makeQuery(id+"F20.imprint","IMPRINT",EDGE,{"derivedFrom":sQuery(id+"F20.wireOp",EDGE,"E77.0")}),1.0]])]});
            var Q11;
            Q11=makeQuery(id+"F20.imprint","IMPRINT",FACE,{"disambiguationData":[TD([[makeQuery(id+"F20.imprint","IMPRINT",EDGE,{"derivedFrom":sQuery(id+"F20.wireOp",EDGE,"E76.0")}),1.0]])]});
            var Q12;
            Q12=makeQuery(id+"F20.imprint","IMPRINT",FACE,{"disambiguationData":[TD([[makeQuery(id+"F20.imprint","IMPRINT",EDGE,{"derivedFrom":sQuery(id+"F20.wireOp",EDGE,"E75.0")}),1.0]])]});
            var Q13;
            Q13=makeQuery(id+"F20.imprint","IMPRINT",FACE,{"disambiguationData":[TD([[makeQuery(id+"F20.imprint","IMPRINT",EDGE,{"derivedFrom":sQuery(id+"F20.wireOp",EDGE,"E74.0")}),1.0]])]});
            extrude(context, id + "F21", {"entities" : qUnion([Q0, Q1, Q2, Q3, Q4, Q5, Q6, Q7, Q8, Q9, Q10, Q11, Q12, Q13]), "operationType" : NewBodyOperationType.REMOVE, "endBound" : BoundingType.UP_TO_NEXT, "oppositeDirection" : true, "depth" : 25 * mm});
        }
    });
